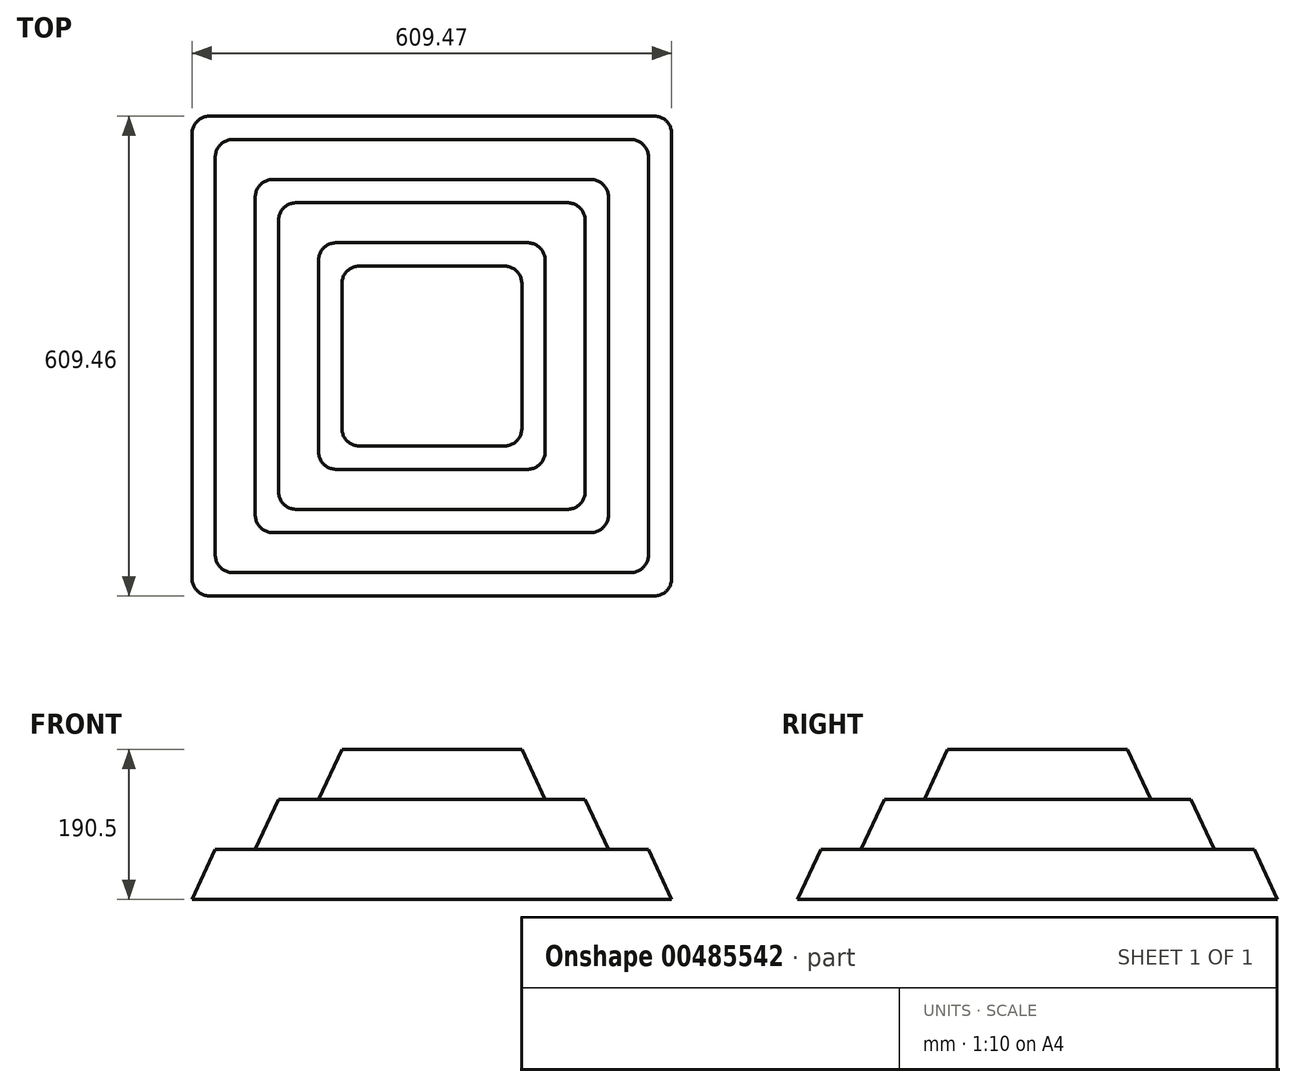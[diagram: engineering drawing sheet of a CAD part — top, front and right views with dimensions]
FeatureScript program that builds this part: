
annotation { "Feature Type Name" : "Feature", "Feature Type Description" : "" }
export const myFeature = defineFeature(function(context is Context, id is Id, definition is map)
    precondition{}
    {
        {
            var Q0;
            Q0=qCreatedBy(makeId("Front.planeOp"),FACE);
            var sketch = newSketch(context, id + "F0", { "sketchPlane" : qUnion([Q0])});
            skLineSegment(sketch, "E0", {"start": v(60.65, 272.15) * mm, "end": v(60.65, -259.19) * mm, "construction": true});
            skLineSegment(sketch, "E1", {"start": v(60.65, -85.6) * mm, "end": v(365.38, -85.6) * mm});
            skLineSegment(sketch, "E2", {"start": v(365.38, -85.6) * mm, "end": v(335.77, -22.1) * mm});
            skLineSegment(sketch, "E3", {"start": v(335.77, -22.1) * mm, "end": v(60.65, -22.1) * mm});
            skLineSegment(sketch, "E4", {"start": v(284.97, -22.1) * mm, "end": v(255.36, 41.4) * mm});
            skLineSegment(sketch, "E5", {"start": v(255.36, 41.4) * mm, "end": v(60.65, 41.4) * mm});
            skLineSegment(sketch, "E6", {"start": v(204.56, 41.4) * mm, "end": v(174.95, 104.9) * mm});
            skLineSegment(sketch, "E7", {"start": v(174.95, 104.9) * mm, "end": v(60.65, 104.9) * mm});
            skLineSegment(sketch, "E8", {"start": v(60.65, 104.9) * mm, "end": v(60.65, -85.6) * mm});
            skLineSegment(sketch, "E9.MirrorCS", {"start": v(60.65, -85.6) * mm, "end": v(-244.09, -85.6) * mm});
            skLineSegment(sketch, "E10.MirrorCS", {"start": v(-214.48, -22.1) * mm, "end": v(60.65, -22.1) * mm});
            skLineSegment(sketch, "E11.MirrorCS", {"start": v(-134.06, 41.4) * mm, "end": v(60.65, 41.4) * mm});
            skLineSegment(sketch, "E12.MirrorCS", {"start": v(-53.65, 104.9) * mm, "end": v(60.65, 104.9) * mm});
            skLineSegment(sketch, "E13.MirrorCS", {"start": v(-244.09, -85.6) * mm, "end": v(-214.48, -22.1) * mm});
            skLineSegment(sketch, "E14.MirrorCS", {"start": v(-163.68, -22.1) * mm, "end": v(-134.06, 41.4) * mm});
            skLineSegment(sketch, "E15.MirrorCS", {"start": v(-83.26, 41.4) * mm, "end": v(-53.65, 104.9) * mm});
            skSolve(sketch);
        }
        {
            var Q0;
            {var subQ3=sQuery(id+"F0.wireOp",EDGE,"E12.MirrorCS");Q0=makeQuery(id+"F0.imprint","IMPRINT",FACE,{"disambiguationData":[TD([[makeQuery(id+"F0.imprint","IMPRINT",EDGE,{"derivedFrom":subQ3}),-1.0]])]});}
            var Q1;
            {var subQ3=sQuery(id+"F0.wireOp",EDGE,"E6");Q1=makeQuery(id+"F0.imprint","IMPRINT",FACE,{"disambiguationData":[TD([[makeQuery(id+"F0.imprint","IMPRINT",EDGE,{"derivedFrom":subQ3}),1.0]])]});}
            var Q2;
            {var subQ4=sQuery(id+"F0.wireOp",EDGE,"E4");Q2=makeQuery(id+"F0.imprint","IMPRINT",FACE,{"disambiguationData":[TD([[makeQuery(id+"F0.imprint","IMPRINT",EDGE,{"derivedFrom":subQ4}),1.0]])]});}
            var Q3;
            {var subQ6=sQuery(id+"F0.wireOp",EDGE,"E14.MirrorCS");Q3=makeQuery(id+"F0.imprint","IMPRINT",FACE,{"disambiguationData":[TD([[makeQuery(id+"F0.imprint","IMPRINT",EDGE,{"derivedFrom":subQ6}),-1.0]])]});}
            var Q4;
            {var subQ5=sQuery(id+"F0.wireOp",EDGE,"E9.MirrorCS");Q4=makeQuery(id+"F0.imprint","IMPRINT",FACE,{"disambiguationData":[TD([[makeQuery(id+"F0.imprint","IMPRINT",EDGE,{"derivedFrom":subQ5}),-1.0]])]});}
            var Q5;
            {var subQ5=sQuery(id+"F0.wireOp",EDGE,"E1");Q5=makeQuery(id+"F0.imprint","IMPRINT",FACE,{"disambiguationData":[TD([[makeQuery(id+"F0.imprint","IMPRINT",EDGE,{"derivedFrom":subQ5}),1.0]])]});}
            extrude(context, id + "F1", {"entities" : qUnion([Q0, Q1, Q2, Q3, Q4, Q5]), "endBound" : BoundingType.SYMMETRIC, "depth" : 975.36 * mm});
        }
        {
            var Q0;
            Q0=qCreatedBy(makeId("Right.planeOp"),FACE);
            var sketch = newSketch(context, id + "F2", { "sketchPlane" : qUnion([Q0])});
            skLineSegment(sketch, "E16", {"start": v(9.8, 273.93) * mm, "end": v(9.8, -257.4) * mm, "construction": true});
            skLineSegment(sketch, "E17", {"start": v(9.8, -85.6) * mm, "end": v(314.54, -85.6) * mm});
            skLineSegment(sketch, "E18", {"start": v(314.54, -85.6) * mm, "end": v(284.93, -22.1) * mm});
            skLineSegment(sketch, "E19", {"start": v(284.93, -22.1) * mm, "end": v(-28.3, -22.1) * mm});
            skLineSegment(sketch, "E20", {"start": v(234.13, -22.1) * mm, "end": v(204.52, 41.4) * mm});
            skLineSegment(sketch, "E21", {"start": v(204.52, 41.4) * mm, "end": v(-28.3, 41.4) * mm});
            skLineSegment(sketch, "E22", {"start": v(153.72, 41.4) * mm, "end": v(124.1, 104.9) * mm});
            skLineSegment(sketch, "E23", {"start": v(124.1, 104.9) * mm, "end": v(9.8, 104.9) * mm});
            skLineSegment(sketch, "E24", {"start": v(9.8, 104.9) * mm, "end": v(9.8, -85.6) * mm});
            skLineSegment(sketch, "E25.MirrorCS", {"start": v(-28.3, -85.6) * mm, "end": v(-396.52, -85.6) * mm});
            skLineSegment(sketch, "E26.MirrorCS", {"start": v(-354.21, -22.1) * mm, "end": v(-15.6, -22.1) * mm});
            skLineSegment(sketch, "E27.MirrorCS", {"start": v(-273.8, 41.4) * mm, "end": v(-28.3, 41.4) * mm});
            skLineSegment(sketch, "E28.MirrorCS", {"start": v(-180.7, 104.9) * mm, "end": v(-28.3, 104.9) * mm});
            skLineSegment(sketch, "E29.MirrorCS", {"start": v(-294.92, -85.6) * mm, "end": v(-265.31, -22.1) * mm});
            skLineSegment(sketch, "E30.MirrorCS", {"start": v(-214.51, -22.1) * mm, "end": v(-184.9, 41.4) * mm});
            skLineSegment(sketch, "E31.MirrorCS", {"start": v(-134.1, 41.4) * mm, "end": v(-104.5, 104.9) * mm});
            skLineSegment(sketch, "E32.0", {"start": v(-487.68, 104.9) * mm, "end": v(487.68, 104.9) * mm});
            skLineSegment(sketch, "E33.0", {"start": v(-487.68, -85.6) * mm, "end": v(487.68, -85.6) * mm});
            skLineSegment(sketch, "E34", {"start": v(-487.68, 104.9) * mm, "end": v(-487.68, -85.6) * mm});
            skLineSegment(sketch, "E35", {"start": v(487.68, 104.9) * mm, "end": v(487.68, -85.6) * mm});
            skLineSegment(sketch, "E36", {"start": v(-28.3, 104.9) * mm, "end": v(9.8, 104.9) * mm});
            skSolve(sketch);
        }
        {
            var Q0;
            {var subQ0=sQuery(id+"F2.wireOp",EDGE,"E29.MirrorCS");Q0=makeQuery(id+"F2.imprint","IMPRINT",FACE,{"disambiguationData":[TD([[makeQuery(id+"F2.imprint","IMPRINT",EDGE,{"derivedFrom":subQ0}),1.0]])]});}
            var Q1;
            {var subQ5=sQuery(id+"F2.wireOp",EDGE,"E18");Q1=makeQuery(id+"F2.imprint","IMPRINT",FACE,{"disambiguationData":[TD([[makeQuery(id+"F2.imprint","IMPRINT",EDGE,{"derivedFrom":subQ5}),-1.0]])]});}
            extrude(context, id + "F3", {"entities" : qUnion([Q0, Q1]), "operationType" : NewBodyOperationType.REMOVE, "endBound" : BoundingType.SYMMETRIC, "oppositeDirection" : true, "depth" : 1087.12 * mm});
        }
        {
            var Q0;
            Q0=makeQuery(id+"F3.boolean.opBoolean","INTERSECT",EDGE,{"derivedFrom":[makeQuery(id+"F1.opExtrude","SWEPT_FACE",FACE,{"disambiguationData":[OSD([sQuery(id+"F0.wireOp",EDGE,"E15.MirrorCS")])]}),makeQuery(id+"F3.opExtrude","SWEPT_FACE",FACE,{"disambiguationData":[OSD([sQuery(id+"F2.wireOp",EDGE,"E22")])]})]});
            var Q1;
            Q1=makeQuery(id+"F3.boolean.opBoolean","INTERSECT",EDGE,{"derivedFrom":[makeQuery(id+"F1.opExtrude","SWEPT_FACE",FACE,{"disambiguationData":[OSD([sQuery(id+"F0.wireOp",EDGE,"E14.MirrorCS")])]}),makeQuery(id+"F3.opExtrude","SWEPT_FACE",FACE,{"disambiguationData":[OSD([sQuery(id+"F2.wireOp",EDGE,"E20")])]})]});
            var Q2;
            Q2=makeQuery(id+"F3.boolean.opBoolean","INTERSECT",EDGE,{"derivedFrom":[makeQuery(id+"F1.opExtrude","SWEPT_FACE",FACE,{"disambiguationData":[OSD([sQuery(id+"F0.wireOp",EDGE,"E13.MirrorCS")])]}),makeQuery(id+"F3.opExtrude","SWEPT_FACE",FACE,{"disambiguationData":[OSD([sQuery(id+"F2.wireOp",EDGE,"E18")])]})]});
            var Q3;
            Q3=makeQuery(id+"F3.boolean.opBoolean","INTERSECT",EDGE,{"derivedFrom":[makeQuery(id+"F1.opExtrude","SWEPT_FACE",FACE,{"disambiguationData":[OSD([sQuery(id+"F0.wireOp",EDGE,"E2")])]}),makeQuery(id+"F3.opExtrude","SWEPT_FACE",FACE,{"disambiguationData":[OSD([sQuery(id+"F2.wireOp",EDGE,"E18")])]})]});
            var Q4;
            Q4=makeQuery(id+"F3.boolean.opBoolean","INTERSECT",EDGE,{"derivedFrom":[makeQuery(id+"F1.opExtrude","SWEPT_FACE",FACE,{"disambiguationData":[OSD([sQuery(id+"F0.wireOp",EDGE,"E4")])]}),makeQuery(id+"F3.opExtrude","SWEPT_FACE",FACE,{"disambiguationData":[OSD([sQuery(id+"F2.wireOp",EDGE,"E20")])]})]});
            var Q5;
            Q5=makeQuery(id+"F3.boolean.opBoolean","INTERSECT",EDGE,{"derivedFrom":[makeQuery(id+"F1.opExtrude","SWEPT_FACE",FACE,{"disambiguationData":[OSD([sQuery(id+"F0.wireOp",EDGE,"E6")])]}),makeQuery(id+"F3.opExtrude","SWEPT_FACE",FACE,{"disambiguationData":[OSD([sQuery(id+"F2.wireOp",EDGE,"E22")])]})]});
            var Q6;
            Q6=makeQuery(id+"F3.boolean.opBoolean","INTERSECT",EDGE,{"derivedFrom":[makeQuery(id+"F1.opExtrude","SWEPT_FACE",FACE,{"disambiguationData":[OSD([sQuery(id+"F0.wireOp",EDGE,"E2")])]}),makeQuery(id+"F3.opExtrude","SWEPT_FACE",FACE,{"disambiguationData":[OSD([sQuery(id+"F2.wireOp",EDGE,"E29.MirrorCS")])]})]});
            var Q7;
            Q7=makeQuery(id+"F3.boolean.opBoolean","INTERSECT",EDGE,{"derivedFrom":[makeQuery(id+"F1.opExtrude","SWEPT_FACE",FACE,{"disambiguationData":[OSD([sQuery(id+"F0.wireOp",EDGE,"E4")])]}),makeQuery(id+"F3.opExtrude","SWEPT_FACE",FACE,{"disambiguationData":[OSD([sQuery(id+"F2.wireOp",EDGE,"E30.MirrorCS")])]})]});
            var Q8;
            Q8=makeQuery(id+"F3.boolean.opBoolean","INTERSECT",EDGE,{"derivedFrom":[makeQuery(id+"F1.opExtrude","SWEPT_FACE",FACE,{"disambiguationData":[OSD([sQuery(id+"F0.wireOp",EDGE,"E6")])]}),makeQuery(id+"F3.opExtrude","SWEPT_FACE",FACE,{"disambiguationData":[OSD([sQuery(id+"F2.wireOp",EDGE,"E31.MirrorCS")])]})]});
            var Q9;
            Q9=makeQuery(id+"F3.boolean.opBoolean","INTERSECT",EDGE,{"derivedFrom":[makeQuery(id+"F1.opExtrude","SWEPT_FACE",FACE,{"disambiguationData":[OSD([sQuery(id+"F0.wireOp",EDGE,"E13.MirrorCS")])]}),makeQuery(id+"F3.opExtrude","SWEPT_FACE",FACE,{"disambiguationData":[OSD([sQuery(id+"F2.wireOp",EDGE,"E29.MirrorCS")])]})]});
            var Q10;
            Q10=makeQuery(id+"F3.boolean.opBoolean","INTERSECT",EDGE,{"derivedFrom":[makeQuery(id+"F1.opExtrude","SWEPT_FACE",FACE,{"disambiguationData":[OSD([sQuery(id+"F0.wireOp",EDGE,"E14.MirrorCS")])]}),makeQuery(id+"F3.opExtrude","SWEPT_FACE",FACE,{"disambiguationData":[OSD([sQuery(id+"F2.wireOp",EDGE,"E30.MirrorCS")])]})]});
            var Q11;
            Q11=makeQuery(id+"F3.boolean.opBoolean","INTERSECT",EDGE,{"derivedFrom":[makeQuery(id+"F1.opExtrude","SWEPT_FACE",FACE,{"disambiguationData":[OSD([sQuery(id+"F0.wireOp",EDGE,"E15.MirrorCS")])]}),makeQuery(id+"F3.opExtrude","SWEPT_FACE",FACE,{"disambiguationData":[OSD([sQuery(id+"F2.wireOp",EDGE,"E31.MirrorCS")])]})]});
            fillet(context, id + "F4", {"entities" : qUnion([Q0, Q1, Q2, Q3, Q4, Q5, Q6, Q7, Q8, Q9, Q10, Q11]), "radius" : 25.4 * mm, "allowEdgeOverflow" : false});
        }
    });
